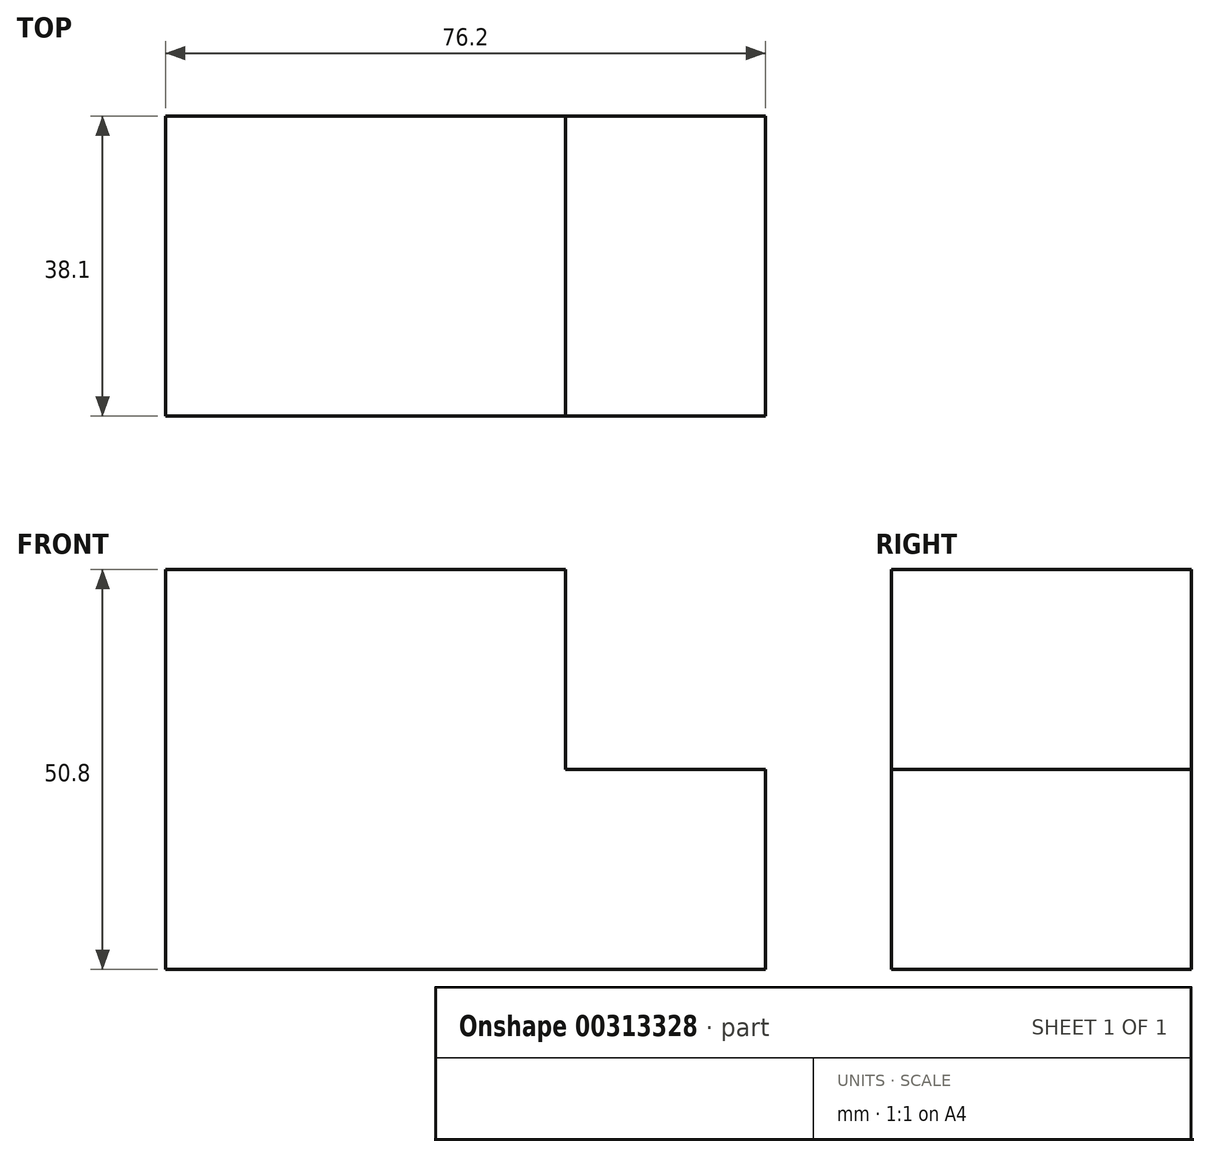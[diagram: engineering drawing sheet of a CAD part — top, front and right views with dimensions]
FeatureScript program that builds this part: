
annotation { "Feature Type Name" : "Feature", "Feature Type Description" : "" }
export const myFeature = defineFeature(function(context is Context, id is Id, definition is map)
    precondition{}
    {
        {
            var Q0;
            Q0=qCreatedBy(makeId("Front.planeOp"),FACE);
            var sketch = newSketch(context, id + "F0", { "sketchPlane" : qUnion([Q0])});
            skLineSegment(sketch, "E0", {"start": v(-39.93, 39.46) * mm, "end": v(10.87, 39.46) * mm});
            skLineSegment(sketch, "E1", {"start": v(10.87, 39.46) * mm, "end": v(10.87, 14.06) * mm});
            skLineSegment(sketch, "E2", {"start": v(10.87, 14.06) * mm, "end": v(36.27, 14.06) * mm});
            skLineSegment(sketch, "E3", {"start": v(36.27, 14.06) * mm, "end": v(36.27, -11.34) * mm});
            skLineSegment(sketch, "E4", {"start": v(36.27, -11.34) * mm, "end": v(-39.93, -11.34) * mm});
            skLineSegment(sketch, "E5", {"start": v(-39.93, 39.46) * mm, "end": v(-39.93, -11.34) * mm});
            skSolve(sketch);
        }
        {
            var Q0;
            Q0=makeQuery(id+"F0.imprint","IMPRINT",FACE,{"disambiguationData":[TD([[makeQuery(id+"F0.imprint","IMPRINT",EDGE,{"derivedFrom":sQuery(id+"F0.wireOp",EDGE,"E0")}),-1.0]])]});
            extrude(context, id + "F1", {"entities" : qUnion([Q0]), "depth" : 38.1 * mm});
        }
    });
